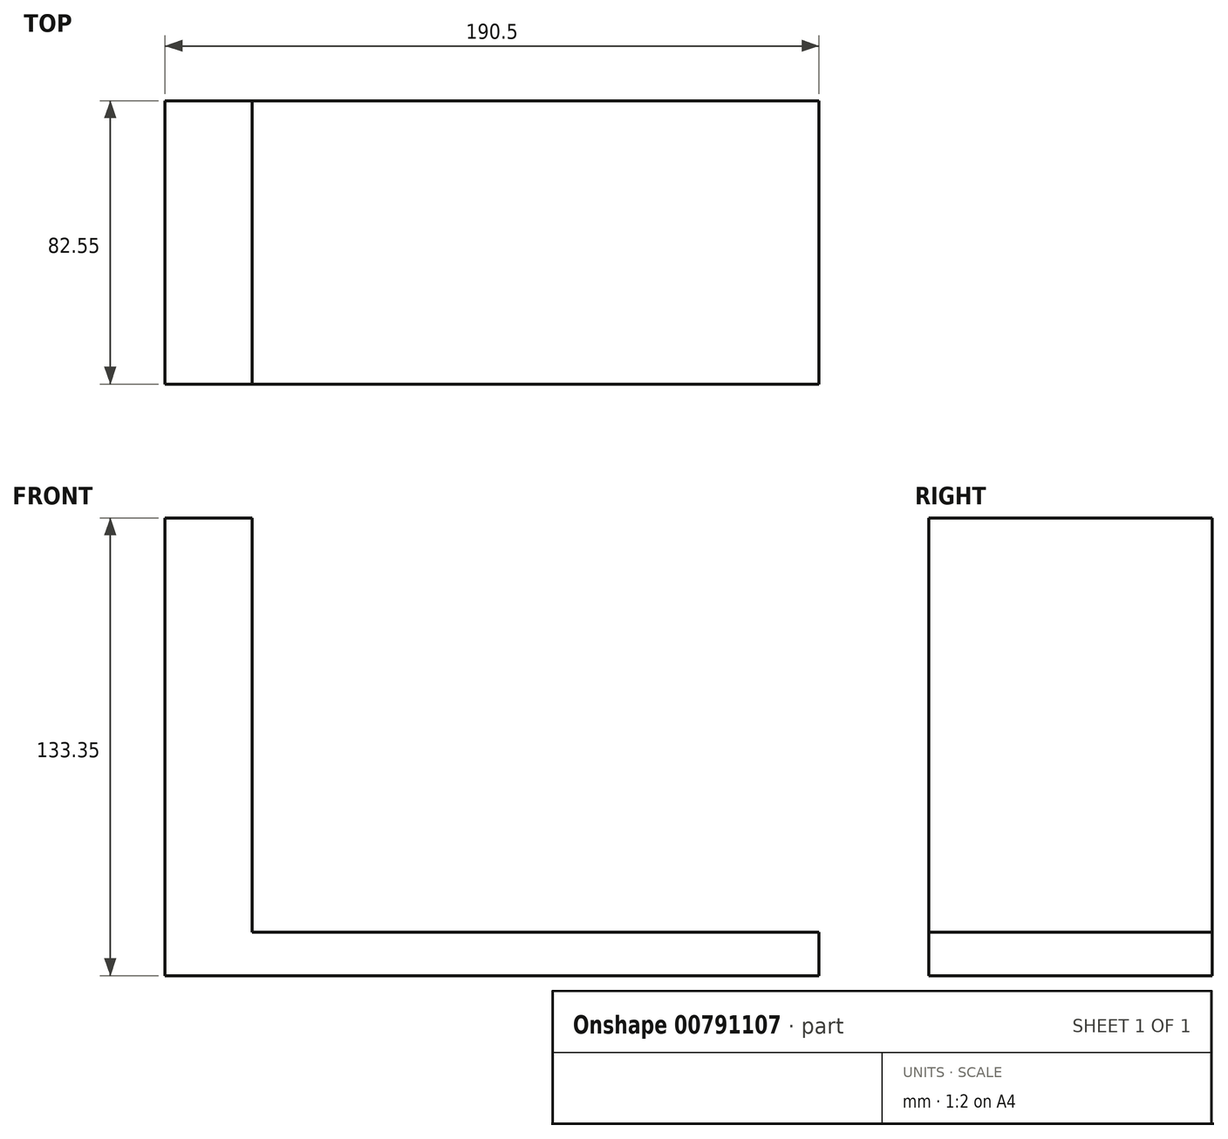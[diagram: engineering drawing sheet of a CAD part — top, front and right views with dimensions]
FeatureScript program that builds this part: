
annotation { "Feature Type Name" : "Feature", "Feature Type Description" : "" }
export const myFeature = defineFeature(function(context is Context, id is Id, definition is map)
    precondition{}
    {
        {
            var Q0;
            Q0=qCreatedBy(makeId("Front.planeOp"),FACE);
            var sketch = newSketch(context, id + "F0", { "sketchPlane" : qUnion([Q0])});
            skLineSegment(sketch, "E0", {"start": v(0, 0) * mm, "end": v(190.5, 0) * mm});
            skLineSegment(sketch, "E1", {"start": v(190.5, 0) * mm, "end": v(190.5, 12.7) * mm});
            skLineSegment(sketch, "E2", {"start": v(190.5, 12.7) * mm, "end": v(25.4, 12.7) * mm});
            skLineSegment(sketch, "E3", {"start": v(0, 0) * mm, "end": v(0, 57.15) * mm});
            skLineSegment(sketch, "E4", {"start": v(0, 57.15) * mm, "end": v(25.4, 57.15) * mm});
            skLineSegment(sketch, "E5", {"start": v(25.4, 57.15) * mm, "end": v(25.4, 12.7) * mm});
            skSolve(sketch);
        }
        {
            var Q0;
            Q0=makeQuery(id+"F0.imprint","IMPRINT",FACE,{"disambiguationData":[TD([[makeQuery(id+"F0.imprint","IMPRINT",EDGE,{"derivedFrom":sQuery(id+"F0.wireOp",EDGE,"E0")}),1.0]])]});
            extrude(context, id + "F1", {"entities" : qUnion([Q0]), "depth" : 25.4 * mm, "offsetDistance" : 25.4 * mm});
        }
        {
            var Q0;
            Q0=makeQuery(id+"F1.opExtrude","CAP_FACE",FACE,{"disambiguationData":[OSD([sQuery(id+"F0.wireOp",EDGE,"E0"),sQuery(id+"F0.wireOp",EDGE,"E1"),sQuery(id+"F0.wireOp",EDGE,"E2"),sQuery(id+"F0.wireOp",EDGE,"E3"),sQuery(id+"F0.wireOp",EDGE,"E4"),sQuery(id+"F0.wireOp",EDGE,"E5")])],"isStart":false});
            extrude(context, id + "F2", {"entities" : qUnion([Q0]), "operationType" : NewBodyOperationType.ADD, "depth" : 57.15 * mm, "offsetDistance" : 25.4 * mm});
        }
        {
            var Q0;
            {var subQ0=sQuery(id+"F0.wireOp",EDGE,"E4");Q0=makeQuery(id+"F2.boolean.opBoolean","MERGE",FACE,{"derivedFrom":[makeQuery(id+"F1.opExtrude","SWEPT_FACE",FACE,{"disambiguationData":[OSD([subQ0])]}),makeQuery(id+"F2.opExtrude","SWEPT_FACE",FACE,{"disambiguationData":[OSD([subQ0])]})]});}
            extrude(context, id + "F3", {"entities" : qUnion([Q0]), "operationType" : NewBodyOperationType.ADD, "depth" : 76.2 * mm, "offsetDistance" : 25.4 * mm});
        }
    });
